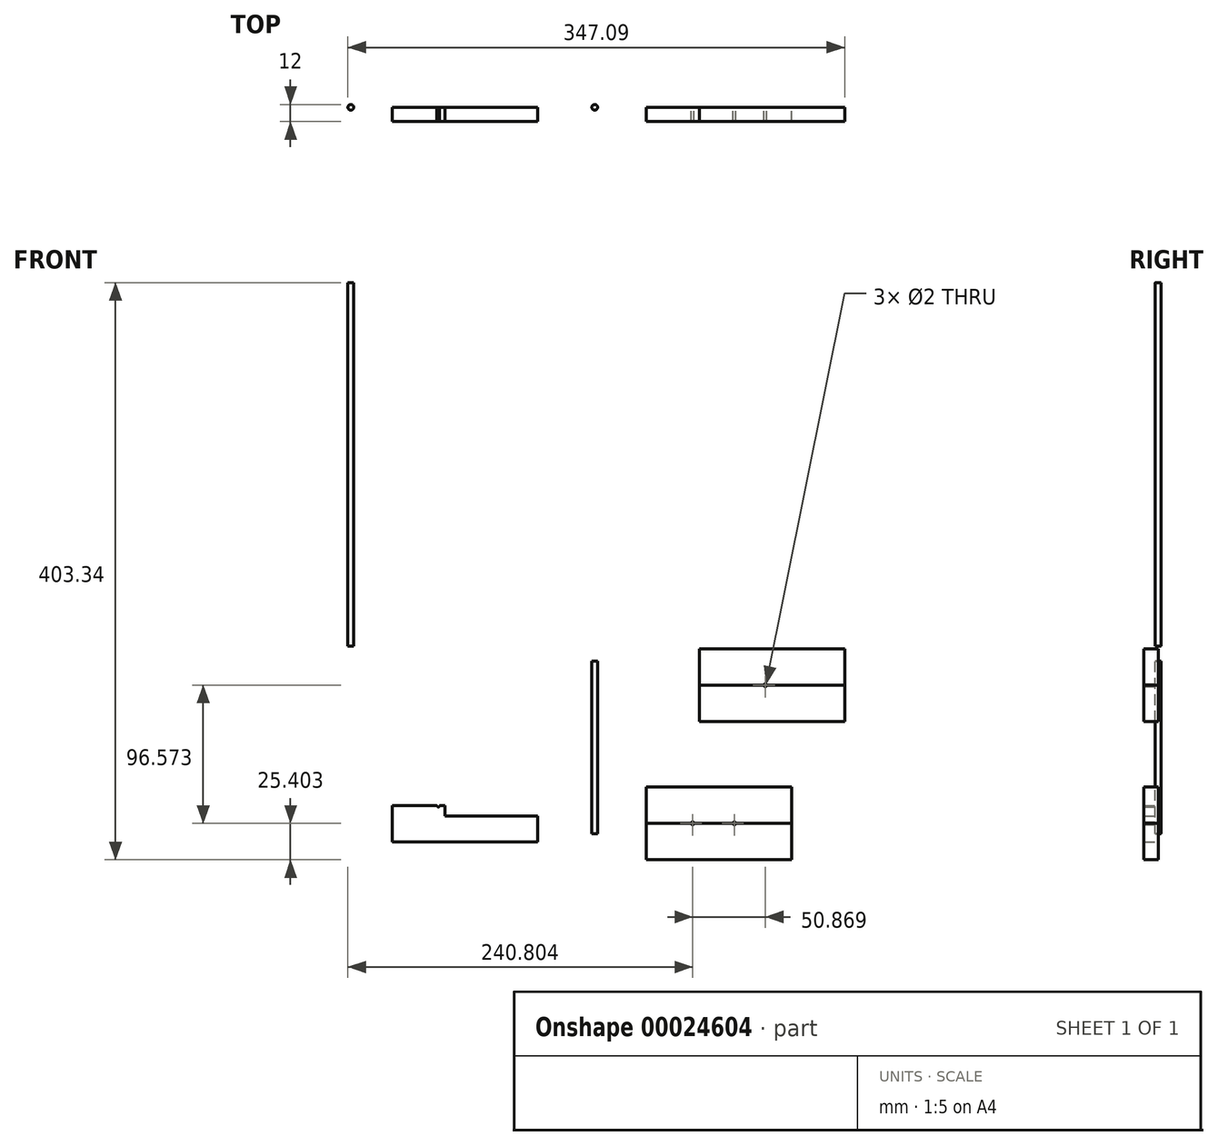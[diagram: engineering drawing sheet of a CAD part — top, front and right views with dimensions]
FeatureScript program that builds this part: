
annotation { "Feature Type Name" : "Feature", "Feature Type Description" : "" }
export const myFeature = defineFeature(function(context is Context, id is Id, definition is map)
    precondition{}
    {
        {
            var Q0;
            Q0=qCreatedBy(makeId("Front.planeOp"),FACE);
            var sketch = newSketch(context, id + "F0", { "sketchPlane" : qUnion([Q0])});
            skLineSegment(sketch, "E0.bottom", {"start": v(-54.83, -89.33) * mm, "end": v(46.77, -89.33) * mm});
            skLineSegment(sketch, "E0.top", {"start": v(-54.83, -140.13) * mm, "end": v(46.77, -140.13) * mm});
            skLineSegment(sketch, "E0.left", {"start": v(-54.83, -89.33) * mm, "end": v(-54.83, -140.13) * mm});
            skLineSegment(sketch, "E0.right", {"start": v(46.77, -89.33) * mm, "end": v(46.77, -140.13) * mm});
            skCircle(sketch, "E1", {"center": v(-22.6, -114.73) * mm, "radius": 1 * mm});
            skLineSegment(sketch, "E2.bottom", {"start": v(-261.4, 263.21) * mm, "end": v(-259.4, 263.21) * mm});
            skLineSegment(sketch, "E2.top", {"start": v(-261.4, 9.21) * mm, "end": v(-259.4, 9.21) * mm});
            skLineSegment(sketch, "E2.left", {"start": v(-261.4, 263.21) * mm, "end": v(-261.4, 9.21) * mm});
            skLineSegment(sketch, "E2.right", {"start": v(-259.4, 263.21) * mm, "end": v(-259.4, 9.21) * mm});
            skLineSegment(sketch, "E3", {"start": v(-22.6, -113.73) * mm, "end": v(-22.6, -115.73) * mm});
            skPoint(sketch, "E4.start.orphan", {"position": v(-54.83, -114.73) * mm});
            skLineSegment(sketch, "E5", {"start": v(-54.83, -114.73) * mm, "end": v(-22.6, -114.73) * mm});
            skLineSegment(sketch, "E6", {"start": v(-22.6, -114.73) * mm, "end": v(5.6, -114.73) * mm});
            skLineSegment(sketch, "E7.bottom", {"start": v(-17.9, 7.25) * mm, "end": v(83.7, 7.25) * mm});
            skLineSegment(sketch, "E7.top", {"start": v(-17.9, -43.55) * mm, "end": v(83.7, -43.55) * mm});
            skLineSegment(sketch, "E7.left", {"start": v(-17.9, 7.25) * mm, "end": v(-17.9, -43.55) * mm});
            skLineSegment(sketch, "E7.right", {"start": v(83.7, 7.25) * mm, "end": v(83.7, -43.55) * mm});
            skLineSegment(sketch, "E8.bottom", {"start": v(-112.74, -136.04) * mm, "end": v(-11.14, -136.04) * mm});
            skLineSegment(sketch, "E8.top", {"start": v(-112.74, -186.84) * mm, "end": v(-11.14, -186.84) * mm});
            skLineSegment(sketch, "E8.left", {"start": v(-112.74, -136.04) * mm, "end": v(-112.74, -186.84) * mm});
            skLineSegment(sketch, "E8.right", {"start": v(-11.14, -136.04) * mm, "end": v(-11.14, -186.84) * mm});
            skCircle(sketch, "E9", {"center": v(28.27, -18.15) * mm, "radius": 1 * mm});
            skCircle(sketch, "E10", {"center": v(-61.94, -161.44) * mm, "radius": 9.8 * mm});
            skLineSegment(sketch, "E11", {"start": v(-112.74, -161.44) * mm, "end": v(-61.94, -161.44) * mm});
            skLineSegment(sketch, "E12.bottom", {"start": v(-90.96, -1.21) * mm, "end": v(-88.96, -1.21) * mm});
            skLineSegment(sketch, "E12.top", {"start": v(-90.96, -121.94) * mm, "end": v(-88.96, -121.94) * mm});
            skLineSegment(sketch, "E12.left", {"start": v(-90.96, -1.21) * mm, "end": v(-90.96, -121.94) * mm});
            skLineSegment(sketch, "E12.right", {"start": v(-88.96, -1.21) * mm, "end": v(-88.96, -121.94) * mm});
            skLineSegment(sketch, "E13", {"start": v(28.26, -17.15) * mm, "end": v(28.27, -19.15) * mm});
            skPoint(sketch, "E14.start.orphan", {"position": v(-17.9, -18.15) * mm});
            skLineSegment(sketch, "E15", {"start": v(-17.9, -18.15) * mm, "end": v(28.27, -18.15) * mm});
            skLineSegment(sketch, "E16", {"start": v(28.27, -18.15) * mm, "end": v(83.7, -18.15) * mm});
            skCircle(sketch, "E17", {"center": v(6.6, -114.73) * mm, "radius": 1 * mm});
            skLineSegment(sketch, "E18.trimOffspring", {"start": v(7.6, -114.73) * mm, "end": v(46.77, -114.73) * mm});
            skLineSegment(sketch, "E19", {"start": v(5.6, -114.73) * mm, "end": v(7.6, -114.73) * mm});
            skLineSegment(sketch, "E20.bottom", {"start": v(-232.48, -76.8) * mm, "end": v(-130.88, -76.8) * mm});
            skLineSegment(sketch, "E20.top", {"start": v(-232.48, -127.6) * mm, "end": v(-130.88, -127.6) * mm});
            skLineSegment(sketch, "E20.left", {"start": v(-232.48, -76.8) * mm, "end": v(-232.48, -127.6) * mm});
            skLineSegment(sketch, "E20.right", {"start": v(-130.88, -76.8) * mm, "end": v(-130.88, -127.6) * mm});
            skCircle(sketch, "E21", {"center": v(-200.25, -102.2) * mm, "radius": 1 * mm});
            skLineSegment(sketch, "E22.bottom", {"start": v(-359.66, 1.56) * mm, "end": v(-357.66, 1.56) * mm});
            skLineSegment(sketch, "E22.top", {"start": v(-359.66, -77) * mm, "end": v(-357.66, -77) * mm});
            skLineSegment(sketch, "E22.left", {"start": v(-359.66, 1.56) * mm, "end": v(-359.66, -77) * mm});
            skLineSegment(sketch, "E22.right", {"start": v(-357.66, 1.56) * mm, "end": v(-357.66, -77) * mm});
            skLineSegment(sketch, "E23", {"start": v(-200.26, -101.2) * mm, "end": v(-200.25, -103.2) * mm});
            skPoint(sketch, "E24.start.orphan", {"position": v(-232.48, -102.2) * mm});
            skLineSegment(sketch, "E25", {"start": v(-232.48, -102.2) * mm, "end": v(-200.25, -102.2) * mm});
            skLineSegment(sketch, "E26", {"start": v(-200.25, -102.2) * mm, "end": v(-172.05, -102.2) * mm});
            skLineSegment(sketch, "E27.bottom", {"start": v(-195.56, -58.9) * mm, "end": v(-93.96, -58.9) * mm});
            skLineSegment(sketch, "E27.top", {"start": v(-195.56, -109.7) * mm, "end": v(-93.96, -109.7) * mm});
            skLineSegment(sketch, "E27.left", {"start": v(-195.56, -58.9) * mm, "end": v(-195.56, -109.7) * mm});
            skLineSegment(sketch, "E27.right", {"start": v(-93.96, -58.9) * mm, "end": v(-93.96, -109.7) * mm});
            skLineSegment(sketch, "E28.bottom", {"start": v(-290.39, -160.04) * mm, "end": v(-188.79, -160.04) * mm});
            skLineSegment(sketch, "E28.top", {"start": v(-290.39, -210.84) * mm, "end": v(-188.79, -210.84) * mm});
            skLineSegment(sketch, "E28.left", {"start": v(-290.39, -160.04) * mm, "end": v(-290.39, -210.84) * mm});
            skLineSegment(sketch, "E28.right", {"start": v(-188.79, -160.04) * mm, "end": v(-188.79, -210.84) * mm});
            skCircle(sketch, "E29", {"center": v(-95.25, -84.3) * mm, "radius": 1 * mm});
            skCircle(sketch, "E30", {"center": v(-239.59, -185.44) * mm, "radius": 9.8 * mm});
            skLineSegment(sketch, "E31", {"start": v(-290.39, -185.44) * mm, "end": v(-239.59, -185.44) * mm});
            skLineSegment(sketch, "E32.bottom", {"start": v(-322.74, -25.2) * mm, "end": v(-320.74, -25.2) * mm});
            skLineSegment(sketch, "E32.top", {"start": v(-322.74, -103.77) * mm, "end": v(-320.74, -103.77) * mm});
            skLineSegment(sketch, "E32.left", {"start": v(-322.74, -25.2) * mm, "end": v(-322.74, -103.77) * mm});
            skLineSegment(sketch, "E32.right", {"start": v(-320.74, -25.2) * mm, "end": v(-320.74, -103.77) * mm});
            skLineSegment(sketch, "E33", {"start": v(-95.27, -83.3) * mm, "end": v(-95.25, -85.3) * mm});
            skPoint(sketch, "E34.start.orphan", {"position": v(-195.56, -84.3) * mm});
            skLineSegment(sketch, "E35", {"start": v(-195.56, -84.3) * mm, "end": v(-95.25, -84.3) * mm});
            skLineSegment(sketch, "E36", {"start": v(-95.25, -84.3) * mm, "end": v(-93.96, -84.3) * mm});
            skCircle(sketch, "E37", {"center": v(-171.05, -102.2) * mm, "radius": 1 * mm});
            skLineSegment(sketch, "E38.trimOffspring", {"start": v(-170.05, -102.2) * mm, "end": v(-130.88, -102.2) * mm});
            skLineSegment(sketch, "E39", {"start": v(-172.05, -102.2) * mm, "end": v(-170.05, -102.2) * mm});
            skSolve(sketch);
        }
        {
            var Q0;
            {var subQ10=sQuery(id+"F0.wireOp",EDGE,"E0.top");Q0=makeQuery(id+"F0.imprint","IMPRINT",FACE,{"disambiguationData":[TD([[makeQuery(id+"F0.imprint","IMPRINT",EDGE,{"derivedFrom":subQ10}),1.0]])]});}
            var Q1;
            {var subQ1=sQuery(id+"F0.wireOp",EDGE,"E0.top");var subQ13=sQuery(id+"F0.wireOp",EDGE,"E0.left");var subQ16=makeQuery(id+"F0.imprint","INTERSECT",VERTEX,{"derivedFrom":[subQ1,subQ13]});Q1=makeQuery(id+"F0.imprint","IMPRINT",FACE,{"disambiguationData":[TD([[makeQuery(id+"F0.imprint","IMPRINT",EDGE,{"disambiguationData":[TD([[subQ16,-1.0]])],"derivedFrom":subQ1}),1.0]])]});}
            var Q2;
            {var subQ10=sQuery(id+"F0.wireOp",EDGE,"E7.top");Q2=makeQuery(id+"F0.imprint","IMPRINT",FACE,{"disambiguationData":[TD([[makeQuery(id+"F0.imprint","IMPRINT",EDGE,{"derivedFrom":subQ10}),1.0]])]});}
            var Q3;
            {var subQ12=sQuery(id+"F0.wireOp",EDGE,"E0.top");var subQ14=sQuery(id+"F0.wireOp",EDGE,"E0.right");var subQ16=makeQuery(id+"F0.imprint","INTERSECT",VERTEX,{"derivedFrom":[subQ12,subQ14]});Q3=makeQuery(id+"F0.imprint","IMPRINT",FACE,{"disambiguationData":[TD([[makeQuery(id+"F0.imprint","IMPRINT",EDGE,{"disambiguationData":[TD([[subQ16,1.0]])],"derivedFrom":subQ12}),-1.0]])]});}
            var Q4;
            {var subQ3=sQuery(id+"F0.wireOp",EDGE,"E8.bottom");Q4=makeQuery(id+"F0.imprint","IMPRINT",FACE,{"disambiguationData":[TD([[makeQuery(id+"F0.imprint","IMPRINT",EDGE,{"derivedFrom":subQ3}),-1.0]])]});}
            var Q5;
            {var subQ0=sQuery(id+"F0.wireOp",EDGE,"E18.trimOffspring");Q5=makeQuery(id+"F0.imprint","IMPRINT",FACE,{"disambiguationData":[TD([[makeQuery(id+"F0.imprint","IMPRINT",EDGE,{"derivedFrom":subQ0}),-1.0]])]});}
            var Q6;
            {var subQ10=sQuery(id+"F0.wireOp",EDGE,"E7.bottom");Q6=makeQuery(id+"F0.imprint","IMPRINT",FACE,{"disambiguationData":[TD([[makeQuery(id+"F0.imprint","IMPRINT",EDGE,{"derivedFrom":subQ10}),-1.0]])]});}
            var Q7;
            {var subQ13=sQuery(id+"F0.wireOp",EDGE,"E0.bottom");Q7=makeQuery(id+"F0.imprint","IMPRINT",FACE,{"disambiguationData":[TD([[makeQuery(id+"F0.imprint","IMPRINT",EDGE,{"derivedFrom":subQ13}),-1.0]])]});}
            var Q8;
            {var subQ13=sQuery(id+"F0.wireOp",EDGE,"E20.top");Q8=makeQuery(id+"F0.imprint","IMPRINT",FACE,{"disambiguationData":[TD([[makeQuery(id+"F0.imprint","IMPRINT",EDGE,{"derivedFrom":subQ13}),1.0]])]});}
            var Q9;
            {var subQ20=sQuery(id+"F0.wireOp",EDGE,"E12.top");Q9=makeQuery(id+"F0.imprint","IMPRINT",FACE,{"disambiguationData":[TD([[makeQuery(id+"F0.imprint","IMPRINT",EDGE,{"derivedFrom":subQ20}),-1.0]])]});}
            extrude(context, id + "F1", {"entities" : qUnion([Q0, Q1, Q2, Q3, Q4, Q5, Q6, Q7, Q8, Q9]), "depth" : 10 * mm});
        }
        {
            var Q0;
            Q0=makeQuery(id+"F0.imprint","IMPRINT",FACE,{"disambiguationData":[TD([[makeQuery(id+"F0.imprint","IMPRINT",EDGE,{"derivedFrom":sQuery(id+"F0.wireOp",EDGE,"E0.bottom")}),-1.0]])]});
            var Q1;
            Q1=makeQuery(id+"F0.imprint","IMPRINT",FACE,{"disambiguationData":[TD([[makeQuery(id+"F0.imprint","IMPRINT",EDGE,{"derivedFrom":sQuery(id+"F0.wireOp",EDGE,"98e749a9-61d1-4376-9f74-d4b30aa28591.bottom")}),-1.0]])]});
            var Q2;
            {var subQ10=sQuery(id+"F0.wireOp",EDGE,"E7.bottom");Q2=makeQuery(id+"F0.imprint","IMPRINT",FACE,{"disambiguationData":[TD([[makeQuery(id+"F0.imprint","IMPRINT",EDGE,{"derivedFrom":subQ10}),-1.0]])]});}
            extrude(context, id + "F2", {"entities" : qUnion([Q0, Q1, Q2]), "depth" : 10 * mm});
        }
        {
            var Q0;
            Q0=makeQuery(id+"F0.imprint","IMPRINT",FACE,{"disambiguationData":[TD([[makeQuery(id+"F0.imprint","IMPRINT",EDGE,{"derivedFrom":sQuery(id+"F0.wireOp",EDGE,"E2.bottom")}),-1.0]])]});
            var Q1;
            Q1=sQuery(id+"F0.wireOp",EDGE,"E2.left");
            revolve(context, id + "F3", {"entities" : qUnion([Q0]), "axis" : qUnion([Q1]), "revolveType" : RevolveType.FULL});
        }
        {
            var Q0;
            Q0=makeQuery(id+"F0.imprint","IMPRINT",FACE,{"disambiguationData":[TD([[makeQuery(id+"F0.imprint","IMPRINT",EDGE,{"derivedFrom":sQuery(id+"F0.wireOp",EDGE,"E12.bottom")}),-1.0]])]});
            var Q1;
            Q1=sQuery(id+"F0.wireOp",EDGE,"E12.left");
            revolve(context, id + "F4", {"entities" : qUnion([Q0]), "axis" : qUnion([Q1]), "revolveType" : RevolveType.FULL});
        }
    });
